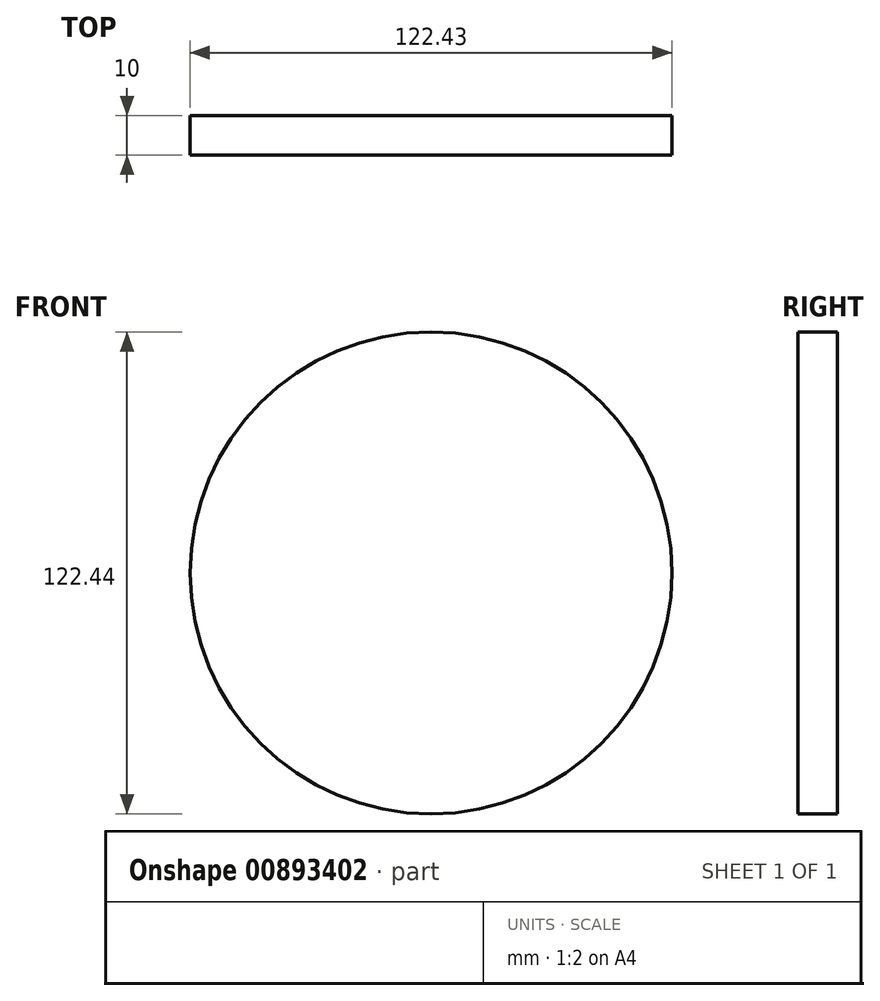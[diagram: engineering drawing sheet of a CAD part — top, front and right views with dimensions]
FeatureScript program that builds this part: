
annotation { "Feature Type Name" : "Feature", "Feature Type Description" : "" }
export const myFeature = defineFeature(function(context is Context, id is Id, definition is map)
    precondition{}
    {
        {
            var Q0;
            Q0=qCreatedBy(makeId("Front.planeOp"),FACE);
            var sketch = newSketch(context, id + "F0", { "sketchPlane" : qUnion([Q0])});
            skCircle(sketch, "E0", {"center": v(-33.7, 20.91) * mm, "radius": 61.22 * mm});
            skSolve(sketch);
        }
        {
            var Q0;
            Q0=makeQuery(id+"F0.imprint","IMPRINT",FACE,{"disambiguationData":[TD([[makeQuery(id+"F0.imprint","IMPRINT",EDGE,{"derivedFrom":sQuery(id+"F0.wireOp",EDGE,"E0")}),1.0]])]});
            extrude(context, id + "F1", {"entities" : qUnion([Q0]), "depth" : 10 * mm, "offsetDistance" : 25.4 * mm});
        }
    });
